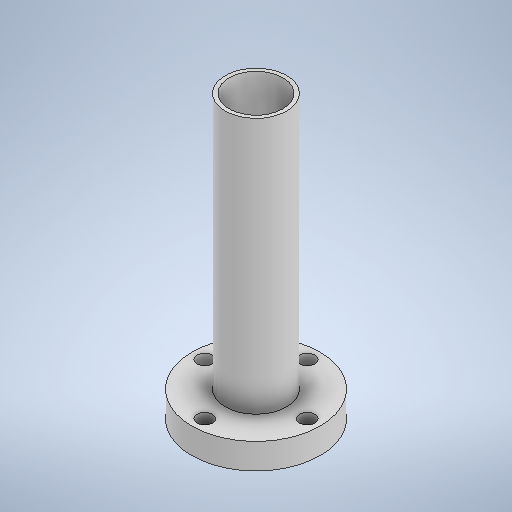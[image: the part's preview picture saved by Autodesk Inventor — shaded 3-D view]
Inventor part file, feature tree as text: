
AUTODESK INVENTOR PART (.ipt)
format: ipt  version: 2025.2 (Build 292293000, 293)  size: 263,680 bytes
history: native  units: mm
features: sketch x4, extrude x2, other x1, hole x1
ambient origin geometry x8: Origin, YZ Plane, XZ Plane, XY Plane, X Axis, Y Axis, Z Axis, Center Point
bodies: Body1 (feature_tree)
feature tree (8):
  other  "Sólido1"
  extrude  "Extrusión1"  Depth=6.0mm
  extrude  "Extrusión2"  Depth=10.0mm TaperAngle=0.0deg
  hole  "Agujero1"  [1 undecoded]
  sketch  "Boceto1"  dims[d0=50.0mm d2=6.0mm]
  sketch  "Boceto - Patrón circular1"  dims[d3=40.0mm d5=360.0deg d7=10.0mm d8=0.0mm]
  sketch  "Boceto2"  dims[d9=24.0mm d10=21.0mm]
  sketch  "Boceto3"  dims[d11=100.0mm d12=0.0mm d13=21.0mm d14=6.0mm d15=4.0mm d16=2.0mm d17=90.0deg d18=8.0mm d19=0.0mm]
note: 1 required parameter value undecoded (feature->parameter linkage not recoverable at this tier; creation-order binding heuristic only, values carry confidence <= 0.55)
